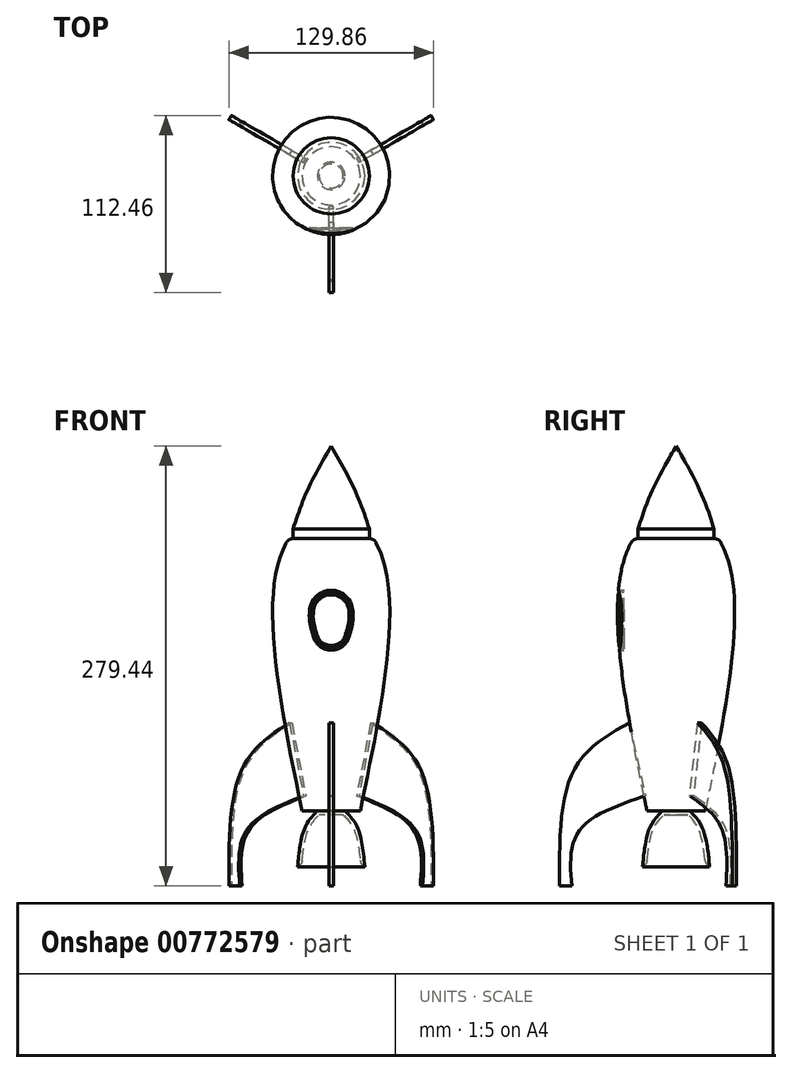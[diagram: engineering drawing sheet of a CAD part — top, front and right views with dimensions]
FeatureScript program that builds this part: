
annotation { "Feature Type Name" : "Feature", "Feature Type Description" : "" }
export const myFeature = defineFeature(function(context is Context, id is Id, definition is map)
    precondition{}
    {
        {
            var Q0;
            Q0=qCreatedBy(makeId("Front.planeOp"),FACE);
            var sketch = newSketch(context, id + "F0", { "sketchPlane" : qUnion([Q0])});
            skLineSegment(sketch, "E0", {"start": v(-18.47, -47.16) * mm, "end": v(0, -47.16) * mm});
            skLineSegment(sketch, "E1", {"start": v(0, -47.16) * mm, "end": v(0, 125.99) * mm});
            skFitSpline(sketch, "E2.trimOffspring", {"points": [v(0, 156.26) * mm, v(-33.74, 109.9) * mm, v(-18.47, -47.16) * mm], "startDerivative": vector(-111.18, -99.1) * mm, "endDerivative": vector(60.1, -291.82) * mm});
            skLineSegment(sketch, "E3", {"start": v(-27.12, 125.99) * mm, "end": v(0, 125.99) * mm});
            skSolve(sketch);
        }
        {
            var Q0;
            Q0=qCreatedBy(makeId("Front.planeOp"),FACE);
            var sketch = newSketch(context, id + "F1", { "sketchPlane" : qUnion([Q0])});
            skFitSpline(sketch, "E4", {"points": [v(-8.7, -46.94) * mm, v(-16.73, -57.72) * mm, v(-21.31, -82.48) * mm], "startDerivative": vector(-21.35, -21.88) * mm, "endDerivative": vector(-4.74, -47.86) * mm});
            skLineSegment(sketch, "E5", {"start": v(-8.7, -46.94) * mm, "end": v(0, -46.94) * mm});
            skLineSegment(sketch, "E6", {"start": v(0, -46.94) * mm, "end": v(0, -79.73) * mm});
            skLineSegment(sketch, "E7", {"start": v(0, -79.73) * mm, "end": v(-21.31, -82.48) * mm});
            skSolve(sketch);
        }
        {
            var Q0;
            Q0=makeQuery(id+"F1.imprint","IMPRINT",FACE,{"disambiguationData":[TD([[makeQuery(id+"F1.imprint","IMPRINT",EDGE,{"derivedFrom":sQuery(id+"F1.wireOp",EDGE,"E4")}),1.0]])]});
            var Q1;
            Q1=sQuery(id+"F1.wireOp",EDGE,"E6");
            revolve(context, id + "F2", {"entities" : qUnion([Q0]), "axis" : qUnion([Q1]), "revolveType" : RevolveType.FULL});
        }
        {
            var Q0;
            Q0=makeQuery(id+"F2.opRevolve","SWEPT_FACE",FACE,{"disambiguationData":[OSD([sQuery(id+"F1.wireOp",EDGE,"E7")])]});
            shell(context, id + "F3", {"entities" : qUnion([Q0]), "thickness" : 2.5 * mm});
        }
        {
            var Q0;
            Q0=qCreatedBy(makeId("Right.planeOp"),FACE);
            var sketch = newSketch(context, id + "F4", { "sketchPlane" : qUnion([Q0])});
            skFitSpline(sketch, "E8", {"points": [v(-29.75, 9) * mm, v(-64.45, -20.3) * mm, v(-74.1, -94.73) * mm], "startDerivative": vector(-92.92, -52.68) * mm, "endDerivative": vector(0.34, -150.7) * mm});
            skLineSegment(sketch, "E9", {"start": v(0, 24.92) * mm, "end": v(0, -98.6) * mm, "construction": true});
            skFitSpline(sketch, "E10", {"points": [v(-66.2, -95.36) * mm, v(-62.02, -60.36) * mm, v(-21.04, -37.93) * mm], "startDerivative": vector(-6.7, 83.04) * mm, "endDerivative": vector(94.64, 32.99) * mm});
            skLineSegment(sketch, "E11", {"start": v(-29.75, 9) * mm, "end": v(-19.48, -37.46) * mm});
            skLineSegment(sketch, "E12", {"start": v(-74.1, -94.73) * mm, "end": v(-66.25, -94.73) * mm});
            skLineSegment(sketch, "E13", {"start": v(-21.04, -37.93) * mm, "end": v(-19.48, -37.46) * mm});
            skPoint(sketch, "E14.orphan", {"position": v(-19.38, -37.93) * mm});
            skSolve(sketch);
        }
        {
            var Q0;
            Q0=makeQuery(id+"F4.imprint","IMPRINT",FACE,{"disambiguationData":[TD([[makeQuery(id+"F4.imprint","IMPRINT",EDGE,{"derivedFrom":sQuery(id+"F4.wireOp",EDGE,"E8")}),1.0]])]});
            extrude(context, id + "F5", {"entities" : qUnion([Q0]), "depth" : 3 * mm, "offsetDistance" : 25 * mm, "symmetric" : true});
        }
        {
            var Q0;
            Q0=makeQuery(id+"F5.opExtrude","SWEPT_BODY",BODY,{"disambiguationData":[OSD([sQuery(id+"F4.wireOp",EDGE,"E8"),sQuery(id+"F4.wireOp",EDGE,"AknD3gLe-WbWz-Pry5-1471-UmxbraZWTH3h"),sQuery(id+"F4.wireOp",EDGE,"97d6337d-07c4-4e44-8112-b2ea29076221")])]});
            var Q1;
            Q1=sQuery(id+"F4.wireOp",EDGE,"E9");
            circularPattern(context, id + "F6", {"entities" : qUnion([Q0]), "axis" : qUnion([Q1]), "angle" : 360 * degree, "instanceCount" : 3, "equalSpace" : true});
        }
        {
            var Q0;
            Q0=makeQuery(id+"F0.imprint","IMPRINT",FACE,{"disambiguationData":[TD([[makeQuery(id+"F0.imprint","IMPRINT",EDGE,{"derivedFrom":sQuery(id+"F0.wireOp",EDGE,"E0")}),1.0]])]});
            var Q1;
            Q1=sQuery(id+"F0.wireOp",EDGE,"E1");
            revolve(context, id + "F7", {"entities" : qUnion([Q0]), "axis" : qUnion([Q1]), "revolveType" : RevolveType.FULL});
        }
        {
            var Q0;
            Q0=qCreatedBy(makeId("Front.planeOp"),FACE);
            var sketch = newSketch(context, id + "F8", { "sketchPlane" : qUnion([Q0])});
            skLineSegment(sketch, "E15", {"start": v(-24.2, 126.12) * mm, "end": v(-24.2, 132) * mm});
            skFitSpline(sketch, "E16", {"points": [v(-24.2, 132) * mm, v(-15.43, 155.88) * mm, v(0, 184.7) * mm], "startDerivative": vector(16.27, 50.18) * mm, "endDerivative": vector(31.8, 55.12) * mm});
            skLineSegment(sketch, "E17", {"start": v(0, 184.7) * mm, "end": v(0, 126.3) * mm});
            skLineSegment(sketch, "E18", {"start": v(0, 126.3) * mm, "end": v(-24.2, 126.12) * mm});
            skSolve(sketch);
        }
        {
            var Q0;
            Q0=makeQuery(id+"F8.imprint","IMPRINT",FACE,{"disambiguationData":[TD([[makeQuery(id+"F8.imprint","IMPRINT",EDGE,{"derivedFrom":sQuery(id+"F8.wireOp",EDGE,"E15")}),-1.0]])]});
            var Q1;
            Q1=sQuery(id+"F8.wireOp",EDGE,"E17");
            revolve(context, id + "F9", {"entities" : qUnion([Q0]), "axis" : qUnion([Q1]), "revolveType" : RevolveType.FULL});
        }
        {
            var Q0;
            Q0=qCreatedBy(makeId("Front.planeOp"),FACE);
            cPlane(context, id + "F10", {"entities" : qUnion([Q0]), "cplaneType" : CPlaneType.OFFSET, "offset" : 33 * mm, "width" : 150 * mm, "height" : 150 * mm});
        }
        {
            var Q0;
            Q0=qCreatedBy(id+"F10.planeOp",FACE);
            var sketch = newSketch(context, id + "F11", { "sketchPlane" : qUnion([Q0])});
            skArc(sketch, "E19", {"start": v(12.56, 80.66) * mm, "mid": v(0, 92.05) * mm, "end": v(-12.56, 80.66) * mm});
            skArc(sketch, "E20", {"start": v(-10.2, 63.64) * mm, "mid": v(0, 56.14) * mm, "end": v(10.2, 63.64) * mm});
            skFitSpline(sketch, "E21", {"points": [v(-12.56, 80.66) * mm, v(-12.7, 74.23) * mm, v(-10.2, 63.64) * mm], "startDerivative": vector(-1.32, -13.55) * mm, "endDerivative": vector(5.18, -16.61) * mm});
            skFitSpline(sketch, "E22.MirrorCS", {"points": [v(12.56, 80.66) * mm, v(12.7, 74.23) * mm, v(10.2, 63.64) * mm], "startDerivative": vector(1.32, -13.55) * mm, "endDerivative": vector(-5.18, -16.61) * mm});
            skArc(sketch, "E23.0", {"start": v(13.65, 80.77) * mm, "mid": v(0, 93.15) * mm, "end": v(-13.65, 80.77) * mm});
            skFitSpline(sketch, "E23.1", {"points": [v(13.65, 80.77) * mm, v(13.7, 80.2) * mm, v(13.83, 79.07) * mm, v(13.92, 77.54) * mm, v(13.93, 76.22) * mm, v(13.9, 75.18) * mm, v(13.8, 74.07) * mm, v(13.6, 72.52) * mm, v(13.2, 70.47) * mm, v(12.6, 67.96) * mm, v(11.92, 65.51) * mm, v(11.46, 64) * mm, v(11.24, 63.31) * mm]});
            skArc(sketch, "E23.2", {"start": v(-11.24, 63.31) * mm, "mid": v(0, 55.04) * mm, "end": v(11.24, 63.31) * mm});
            skFitSpline(sketch, "E23.3", {"points": [v(-13.65, 80.77) * mm, v(-13.7, 80.2) * mm, v(-13.83, 79.07) * mm, v(-13.92, 77.54) * mm, v(-13.93, 76.22) * mm, v(-13.9, 75.18) * mm, v(-13.8, 74.07) * mm, v(-13.6, 72.52) * mm, v(-13.2, 70.47) * mm, v(-12.6, 67.96) * mm, v(-11.92, 65.51) * mm, v(-11.46, 64) * mm, v(-11.24, 63.31) * mm]});
            skSolve(sketch);
        }
        {
            var Q0;
            Q0=qSketchRegion(id+"F11",true);
            extrude(context, id + "F12", {"entities" : qUnion([Q0]), "operationType" : NewBodyOperationType.REMOVE, "endBound" : BoundingType.UP_TO_NEXT, "depth" : 25 * mm, "offsetDistance" : 25 * mm});
        }
        {
            var Q0;
            Q0=makeQuery(id+"F12.boolean.opBoolean","SPLIT",FACE,{"disambiguationData":[TD([makeQuery(id+"F12.opExtrude","SWEPT_FACE",FACE,{"disambiguationData":[OSD([sQuery(id+"F11.wireOp",EDGE,"E19")])]})])],"derivedFrom":makeQuery(id+"F7.opRevolve","SWEPT_FACE",FACE,{"disambiguationData":[OSD([sQuery(id+"F0.wireOp",EDGE,"E2.trimOffspring")])]})});
            fillet(context, id + "F13", {"entities" : qUnion([Q0]), "radius" : 2 * mm, "tangentPropagation" : true, "allowEdgeOverflow" : false});
        }
        {
            var Q0;
            Q0=makeQuery(id+"F7.opRevolve","SWEPT_EDGE",EDGE,{"disambiguationData":[OSD([sQuery(id+"F0.wireOp",EDGE,"E2.trimOffspring"),sQuery(id+"F0.wireOp",EDGE,"E3")])]});
            fillet(context, id + "F14", {"entities" : qUnion([Q0]), "radius" : 5 * mm, "tangentPropagation" : true, "allowEdgeOverflow" : false});
        }
        {
            var Q0;
            Q0=makeQuery(id+"F3.opShell","OFFSET_EDGE",EDGE,{"disambiguationData":[OSD([sQuery(id+"F1.wireOp",EDGE,"E4"),sQuery(id+"F1.wireOp",EDGE,"E7")])]});
            fillet(context, id + "F15", {"entities" : qUnion([Q0]), "radius" : 5 * mm, "tangentPropagation" : true, "allowEdgeOverflow" : false});
        }
    });
